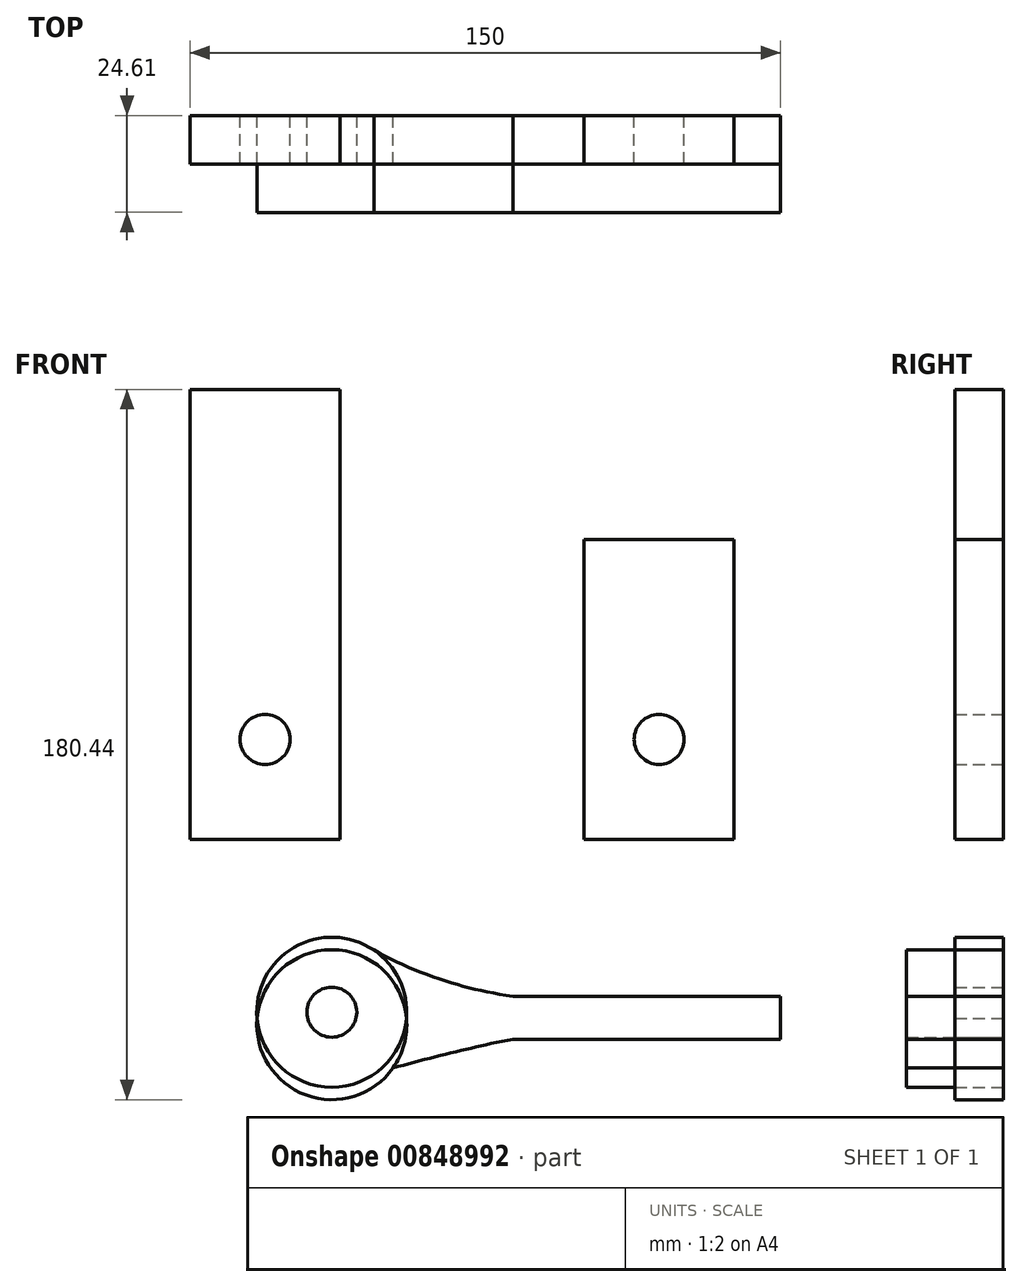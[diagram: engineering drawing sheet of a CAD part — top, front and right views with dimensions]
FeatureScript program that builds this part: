
annotation { "Feature Type Name" : "Feature", "Feature Type Description" : "" }
export const myFeature = defineFeature(function(context is Context, id is Id, definition is map)
    precondition{}
    {
        {
            var Q0;
            Q0=qCreatedBy(makeId("Front.planeOp"),FACE);
            var sketch = newSketch(context, id + "F0", { "sketchPlane" : qUnion([Q0])});
            skLineSegment(sketch, "E0.bottom", {"start": v(-36, 88.9) * mm, "end": v(2.1, 88.9) * mm});
            skLineSegment(sketch, "E0.top", {"start": v(-36, -25.4) * mm, "end": v(2.1, -25.4) * mm});
            skLineSegment(sketch, "E0.left", {"start": v(-36, 88.9) * mm, "end": v(-36, -25.4) * mm});
            skLineSegment(sketch, "E0.right", {"start": v(2.1, 88.9) * mm, "end": v(2.1, -25.4) * mm});
            skCircle(sketch, "E1", {"center": v(-16.95, 0) * mm, "radius": 6.35 * mm});
            skLineSegment(sketch, "E2.bottom", {"start": v(64.11, -25.4) * mm, "end": v(102.21, -25.4) * mm});
            skLineSegment(sketch, "E2.top", {"start": v(64.11, 50.8) * mm, "end": v(102.21, 50.8) * mm});
            skLineSegment(sketch, "E2.left", {"start": v(64.11, -25.4) * mm, "end": v(64.11, 50.8) * mm});
            skLineSegment(sketch, "E2.right", {"start": v(102.21, -25.4) * mm, "end": v(102.21, 50.8) * mm});
            skCircle(sketch, "E3", {"center": v(83.16, 0) * mm, "radius": 6.35 * mm});
            skPoint(sketch, "E3.centerSnap0", {"position": v(83.16, -25.4) * mm});
            skCircle(sketch, "E4", {"center": v(0, -69.31) * mm, "radius": 19.05 * mm});
            skLineSegment(sketch, "E5", {"start": v(18.61, -65.26) * mm, "end": v(114, -65.26) * mm});
            skLineSegment(sketch, "E6", {"start": v(114, -65.26) * mm, "end": v(114, -76.27) * mm});
            skLineSegment(sketch, "E7", {"start": v(114, -76.27) * mm, "end": v(17.73, -76.27) * mm});
            skFitSpline(sketch, "E8", {"points": [v(10.67, -53.53) * mm, v(28.41, -61.23) * mm, v(46.01, -65.26) * mm], "startDerivative": vector(30.58, -18.06) * mm, "endDerivative": vector(39.98, -5.55) * mm});
            skFitSpline(sketch, "E9", {"points": [v(10.67, -85.1) * mm, v(28.41, -80.14) * mm, v(46.01, -76.27) * mm], "startDerivative": vector(31.36, 11.26) * mm, "endDerivative": vector(39.17, 6.47) * mm});
            skCircle(sketch, "E10", {"center": v(0, -69.31) * mm, "radius": 6.35 * mm});
            skCircle(sketch, "E11", {"center": v(0, -72.49) * mm, "radius": 19.05 * mm});
            skSolve(sketch);
        }
        {
            var Q0;
            Q0=makeQuery(id+"F0.imprint","IMPRINT",FACE,{"disambiguationData":[TD([[makeQuery(id+"F0.imprint","IMPRINT",EDGE,{"derivedFrom":sQuery(id+"F0.wireOp",EDGE,"E0.bottom")}),-1.0]])]});
            var Q1;
            Q1=makeQuery(id+"F0.imprint","IMPRINT",FACE,{"disambiguationData":[TD([[makeQuery(id+"F0.imprint","IMPRINT",EDGE,{"derivedFrom":sQuery(id+"F0.wireOp",EDGE,"E2.bottom")}),1.0]])]});
            var Q2;
            {var subQ0=sQuery(id+"F0.wireOp",EDGE,"E4");var subQ1=makeQuery(id+"F0.imprint","INTERSECT",VERTEX,{"derivedFrom":[subQ0,sQuery(id+"F0.wireOp",EDGE,"E5")]});Q2=makeQuery(id+"F0.imprint","IMPRINT",FACE,{"disambiguationData":[TD([[makeQuery(id+"F0.imprint","IMPRINT",EDGE,{"disambiguationData":[TD([[subQ1,-1.0]])],"derivedFrom":subQ0}),1.0]])]});}
            var Q3;
            Q3=makeQuery(id+"F0.imprint","IMPRINT",FACE,{"disambiguationData":[TD([[makeQuery(id+"F0.imprint","IMPRINT",EDGE,{"derivedFrom":sQuery(id+"F0.wireOp",EDGE,"E10")}),-1.0]])]});
            var Q4;
            {var subQ0=sQuery(id+"F0.wireOp",EDGE,"E7");var subQ1=sQuery(id+"F0.wireOp",EDGE,"E4");var subQ2=makeQuery(id+"F0.imprint","INTERSECT",VERTEX,{"derivedFrom":[subQ1,subQ0]});Q4=makeQuery(id+"F0.imprint","IMPRINT",FACE,{"disambiguationData":[TD([[makeQuery(id+"F0.imprint","IMPRINT",EDGE,{"disambiguationData":[TD([[subQ2,1.0]])],"derivedFrom":subQ1}),-1.0]])]});}
            var Q5;
            {var subQ0=sQuery(id+"F0.wireOp",EDGE,"E9");var subQ1=sQuery(id+"F0.wireOp",EDGE,"E4");var subQ2=makeQuery(id+"F0.imprint","INTERSECT",VERTEX,{"derivedFrom":[subQ1,subQ0]});Q5=makeQuery(id+"F0.imprint","IMPRINT",FACE,{"disambiguationData":[TD([[makeQuery(id+"F0.imprint","IMPRINT",EDGE,{"disambiguationData":[TD([[subQ2,1.0]])],"derivedFrom":subQ1}),-1.0]])]});}
            var Q6;
            {var subQ0=sQuery(id+"F0.wireOp",EDGE,"E7");var subQ1=sQuery(id+"F0.wireOp",EDGE,"E4");var subQ2=makeQuery(id+"F0.imprint","INTERSECT",VERTEX,{"derivedFrom":[subQ1,subQ0]});Q6=makeQuery(id+"F0.imprint","IMPRINT",FACE,{"disambiguationData":[TD([[makeQuery(id+"F0.imprint","IMPRINT",EDGE,{"disambiguationData":[TD([[subQ2,-1.0]])],"derivedFrom":subQ1}),-1.0]])]});}
            var Q7;
            {var subQ3=sQuery(id+"F0.wireOp",EDGE,"E8");Q7=makeQuery(id+"F0.imprint","IMPRINT",FACE,{"disambiguationData":[TD([[makeQuery(id+"F0.imprint","IMPRINT",EDGE,{"derivedFrom":subQ3}),-1.0]])]});}
            var Q8;
            {var subQ0=sQuery(id+"F0.wireOp",EDGE,"E6");Q8=makeQuery(id+"F0.imprint","IMPRINT",FACE,{"disambiguationData":[TD([[makeQuery(id+"F0.imprint","IMPRINT",EDGE,{"derivedFrom":subQ0}),-1.0]])]});}
            var Q9;
            {var subQ0=sQuery(id+"F0.wireOp",EDGE,"E9");var subQ1=sQuery(id+"F0.wireOp",EDGE,"E7");var subQ2=makeQuery(id+"F0.imprint","INTERSECT",VERTEX,{"derivedFrom":[subQ1,subQ0]});Q9=makeQuery(id+"F0.imprint","IMPRINT",FACE,{"disambiguationData":[TD([[makeQuery(id+"F0.imprint","IMPRINT",EDGE,{"disambiguationData":[TD([[subQ2,-1.0]])],"derivedFrom":subQ1}),1.0]])]});}
            extrude(context, id + "F1", {"entities" : qUnion([Q0, Q1, Q2, Q3, Q4, Q5, Q6, Q7, Q8, Q9]), "depth" : 12.3 * mm, "offsetDistance" : 25.4 * mm});
        }
        {
            var Q0;
            Q0=makeQuery(id+"F0.imprint","IMPRINT",FACE,{"disambiguationData":[TD([[makeQuery(id+"F0.imprint","IMPRINT",EDGE,{"derivedFrom":sQuery(id+"F0.wireOp",EDGE,"E10")}),-1.0]])]});
            var Q1;
            {var subQ0=sQuery(id+"F0.wireOp",EDGE,"E6");Q1=makeQuery(id+"F0.imprint","IMPRINT",FACE,{"disambiguationData":[TD([[makeQuery(id+"F0.imprint","IMPRINT",EDGE,{"derivedFrom":subQ0}),-1.0]])]});}
            var Q2;
            {var subQ3=sQuery(id+"F0.wireOp",EDGE,"E8");Q2=makeQuery(id+"F0.imprint","IMPRINT",FACE,{"disambiguationData":[TD([[makeQuery(id+"F0.imprint","IMPRINT",EDGE,{"derivedFrom":subQ3}),-1.0]])]});}
            var Q3;
            {var subQ3=sQuery(id+"F0.wireOp",EDGE,"E9");Q3=makeQuery(id+"F0.imprint","IMPRINT",FACE,{"disambiguationData":[TD([[makeQuery(id+"F0.imprint","IMPRINT",EDGE,{"derivedFrom":subQ3}),1.0]])]});}
            extrude(context, id + "F2", {"entities" : qUnion([Q0, Q1, Q2, Q3]), "depth" : 24.6 * mm, "offsetDistance" : 25.4 * mm});
        }
    });
